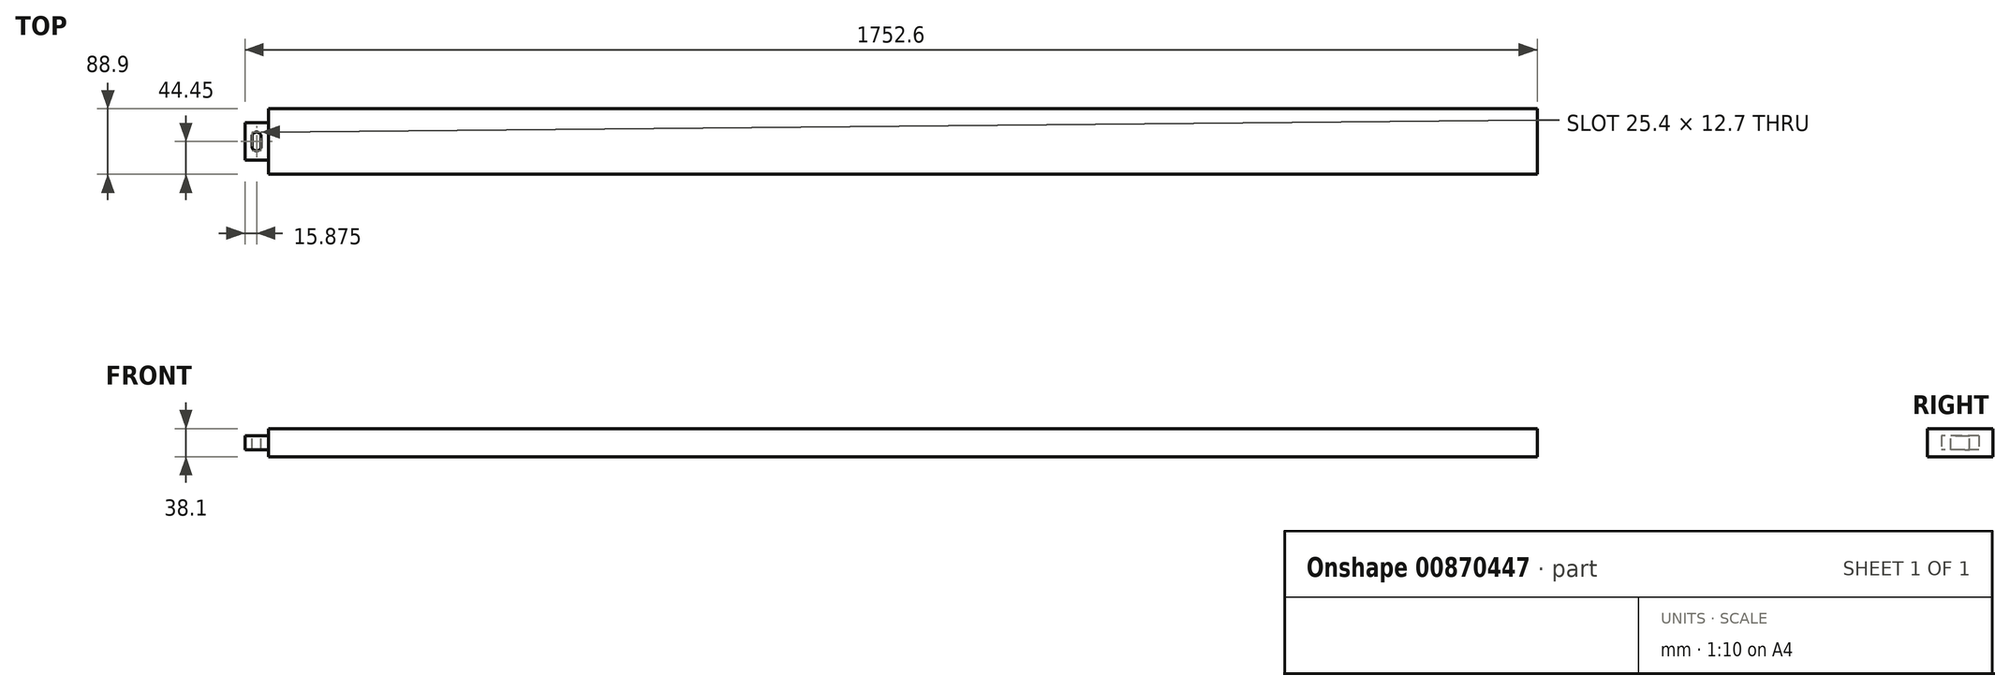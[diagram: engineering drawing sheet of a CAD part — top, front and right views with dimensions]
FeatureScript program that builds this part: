
annotation { "Feature Type Name" : "Feature", "Feature Type Description" : "" }
export const myFeature = defineFeature(function(context is Context, id is Id, definition is map)
    precondition{}
    {
        {
            var Q0;
            Q0=qCreatedBy(makeId("Right.planeOp"),FACE);
            var sketch = newSketch(context, id + "F0", { "sketchPlane" : qUnion([Q0])});
            skLineSegment(sketch, "E0.bottom", {"start": v(44.45, 19.05) * mm, "end": v(-44.45, 19.05) * mm});
            skLineSegment(sketch, "E0.top", {"start": v(44.45, -19.05) * mm, "end": v(-44.45, -19.05) * mm});
            skLineSegment(sketch, "E0.left", {"start": v(44.45, 19.05) * mm, "end": v(44.45, -19.05) * mm});
            skLineSegment(sketch, "E0.right", {"start": v(-44.45, 19.05) * mm, "end": v(-44.45, -19.05) * mm});
            skPoint(sketch, "E0.middle", {"position": v(0, 0) * mm});
            skSolve(sketch);
        }
        {
            var Q0;
            Q0=makeQuery(id+"F0.imprint","IMPRINT",FACE,{"disambiguationData":[TD([[makeQuery(id+"F0.imprint","IMPRINT",EDGE,{"derivedFrom":sQuery(id+"F0.wireOp",EDGE,"E0.bottom")}),1.0]])]});
            extrude(context, id + "F1", {"entities" : qUnion([Q0]), "depth" : 1752.6 * mm, "offsetDistance" : 25.4 * mm});
        }
        {
            var Q0;
            Q0=makeQuery(id+"F1.opExtrude","CAP_FACE",FACE,{"disambiguationData":[OSD([sQuery(id+"F0.wireOp",EDGE,"E0.bottom"),sQuery(id+"F0.wireOp",EDGE,"E0.top"),sQuery(id+"F0.wireOp",EDGE,"E0.left"),sQuery(id+"F0.wireOp",EDGE,"E0.right")])],"isStart":true});
            var Q1;
            Q1=makeQuery(id+"F1.opExtrude","CAP_FACE",FACE,{"disambiguationData":[OSD([sQuery(id+"F0.wireOp",EDGE,"E0.bottom"),sQuery(id+"F0.wireOp",EDGE,"E0.top"),sQuery(id+"F0.wireOp",EDGE,"E0.left"),sQuery(id+"F0.wireOp",EDGE,"E0.right")])],"isStart":false});
            cPlane(context, id + "F2", {"entities" : qUnion([Q0, Q1]), "cplaneType" : CPlaneType.MID_PLANE, "offset" : 25.4 * mm, "width" : 152.4 * mm, "height" : 152.4 * mm});
        }
        {
            var Q0;
            Q0=makeQuery(id+"F1.opExtrude","CAP_FACE",FACE,{"disambiguationData":[OSD([sQuery(id+"F0.wireOp",EDGE,"E0.bottom"),sQuery(id+"F0.wireOp",EDGE,"E0.top"),sQuery(id+"F0.wireOp",EDGE,"E0.left"),sQuery(id+"F0.wireOp",EDGE,"E0.right")])],"isStart":true});
            var sketch = newSketch(context, id + "F3", { "sketchPlane" : qUnion([Q0])});
            skLineSegment(sketch, "E1.bottom", {"start": v(-25.4, 9.53) * mm, "end": v(25.4, 9.52) * mm});
            skLineSegment(sketch, "E1.top", {"start": v(-25.4, -9.52) * mm, "end": v(25.4, -9.53) * mm});
            skLineSegment(sketch, "E1.left", {"start": v(-25.4, 9.53) * mm, "end": v(-25.4, -9.52) * mm});
            skLineSegment(sketch, "E1.right", {"start": v(25.4, 9.52) * mm, "end": v(25.4, -9.53) * mm});
            skPoint(sketch, "E1.middle", {"position": v(0, 0) * mm});
            skSolve(sketch);
        }
        {
            var Q0;
            Q0=makeQuery(id+"F3.imprint","IMPRINT",FACE,{"disambiguationData":[TD([[makeQuery(id+"F3.imprint","IMPRINT",EDGE,{"derivedFrom":sQuery(id+"F3.wireOp",EDGE,"E1.bottom")}),1.0]])]});
            extrude(context, id + "F4", {"entities" : qUnion([Q0]), "operationType" : NewBodyOperationType.REMOVE, "oppositeDirection" : true, "depth" : 31.75 * mm, "offsetDistance" : 25.4 * mm});
        }
        {
            var Q0;
            Q0=makeQuery(id+"F4.boolean.opBoolean","COPY",FACE,{"derivedFrom":makeQuery(id+"F4.opExtrude","SWEPT_FACE",FACE,{"disambiguationData":[OSD([sQuery(id+"F3.wireOp",EDGE,"E1.bottom")])]})});
            var sketch = newSketch(context, id + "F5", { "sketchPlane" : qUnion([Q0])});
            skLineSegment(sketch, "E2", {"start": v(9.53, -6.35) * mm, "end": v(9.53, 6.35) * mm});
            skArc(sketch, "E3", {"start": v(9.53, 6.35) * mm, "mid": v(15.88, 12.7) * mm, "end": v(22.23, 6.35) * mm});
            skLineSegment(sketch, "E4", {"start": v(22.23, 6.35) * mm, "end": v(22.23, -6.35) * mm});
            skArc(sketch, "E5", {"start": v(9.53, -6.35) * mm, "mid": v(15.88, -12.7) * mm, "end": v(22.23, -6.35) * mm});
            skLineSegment(sketch, "E6", {"start": v(-9.2, 0) * mm, "end": v(45.47, 0) * mm, "construction": true});
            skLineSegment(sketch, "E7", {"start": v(15.88, 113.32) * mm, "end": v(15.88, -122.57) * mm, "construction": true});
            skSolve(sketch);
        }
        {
            var Q0;
            Q0=makeQuery(id+"F5.imprint","IMPRINT",FACE,{"disambiguationData":[TD([[makeQuery(id+"F5.imprint","IMPRINT",EDGE,{"derivedFrom":sQuery(id+"F5.wireOp",EDGE,"E2")}),-1.0]])]});
            extrude(context, id + "F6", {"entities" : qUnion([Q0]), "operationType" : NewBodyOperationType.REMOVE, "endBound" : BoundingType.THROUGH_ALL, "oppositeDirection" : true, "depth" : 25.4 * mm, "offsetDistance" : 25.4 * mm});
        }
    });
